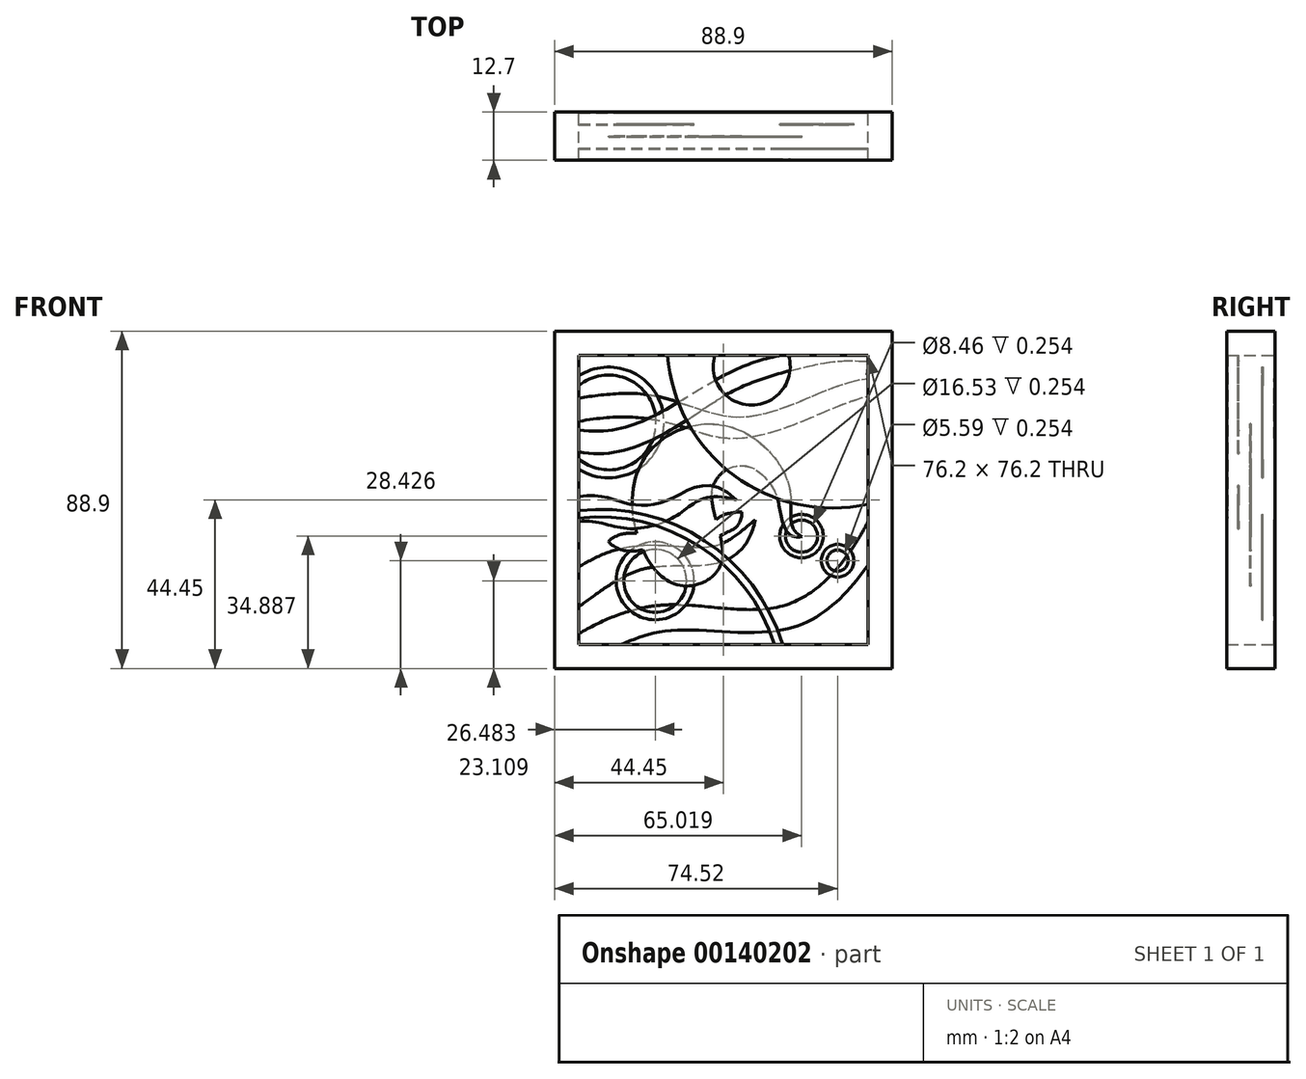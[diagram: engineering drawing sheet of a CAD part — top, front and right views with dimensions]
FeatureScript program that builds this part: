
annotation { "Feature Type Name" : "Feature", "Feature Type Description" : "" }
export const myFeature = defineFeature(function(context is Context, id is Id, definition is map)
    precondition{}
    {
        {
            var Q0;
            Q0=qCreatedBy(makeId("Front.planeOp"),FACE);
            cPlane(context, id + "F0", {"entities" : qUnion([Q0]), "cplaneType" : CPlaneType.OFFSET, "offset" : 3.17 * mm, "width" : 152.4 * mm, "height" : 152.4 * mm});
        }
        {
            var Q0;
            Q0=qCreatedBy(id+"F0.planeOp",FACE);
            cPlane(context, id + "F1", {"entities" : qUnion([Q0]), "cplaneType" : CPlaneType.OFFSET, "offset" : 3.17 * mm, "width" : 152.4 * mm, "height" : 152.4 * mm});
        }
        {
            var Q0;
            Q0=qCreatedBy(id+"F1.planeOp",FACE);
            cPlane(context, id + "F2", {"entities" : qUnion([Q0]), "cplaneType" : CPlaneType.OFFSET, "offset" : 3.17 * mm, "width" : 152.4 * mm, "height" : 152.4 * mm});
        }
        {
            var Q0;
            Q0=qCreatedBy(id+"F2.planeOp",FACE);
            cPlane(context, id + "F3", {"entities" : qUnion([Q0]), "cplaneType" : CPlaneType.OFFSET, "offset" : 3.17 * mm, "width" : 152.4 * mm, "height" : 152.4 * mm});
        }
        {
            var Q0;
            Q0=qCreatedBy(makeId("Front.planeOp"),FACE);
            var sketch = newSketch(context, id + "F4", { "sketchPlane" : qUnion([Q0])});
            skLineSegment(sketch, "E0.bottom", {"start": v(-38.1, 38.1) * mm, "end": v(38.1, 38.1) * mm});
            skLineSegment(sketch, "E0.top", {"start": v(-38.1, -38.1) * mm, "end": v(38.1, -38.1) * mm});
            skLineSegment(sketch, "E0.left", {"start": v(-38.1, 38.1) * mm, "end": v(-38.1, -38.1) * mm});
            skLineSegment(sketch, "E0.right", {"start": v(38.1, 38.1) * mm, "end": v(38.1, -38.1) * mm});
            skLineSegment(sketch, "E1", {"start": v(-38.1, 38.1) * mm, "end": v(38.1, -38.1) * mm, "construction": true});
            skFitSpline(sketch, "E2", {"points": [v(-38.1, -35.27) * mm, v(-14.25, -27.64) * mm, v(17.02, -27.5) * mm, v(38.1, -5.66) * mm], "startDerivative": vector(70.4, 40.4) * mm, "endDerivative": vector(39.04, 77.61) * mm});
            skFitSpline(sketch, "E3", {"points": [v(-38.1, -28.14) * mm, v(-20.93, -18.19) * mm, v(-1.94, -16.72) * mm, v(8.35, -5.22) * mm], "startDerivative": vector(44.97, 31.21) * mm, "endDerivative": vector(12.34, 67.57) * mm});
            skFitSpline(sketch, "E4", {"points": [v(-38.1, -17.76) * mm, v(-22.26, -12.04) * mm, v(-4.48, -12.44) * mm, v(8.35, -5.22) * mm], "startDerivative": vector(39.42, 26) * mm, "endDerivative": vector(58.43, 50.8) * mm});
            skFitSpline(sketch, "E5", {"points": [v(-38.1, 26.81) * mm, v(-18.3, 27.46) * mm, v(3.15, 21.85) * mm, v(23.34, 27.3) * mm, v(38.1, 31.97) * mm], "startDerivative": vector(68.65, 10.07) * mm, "endDerivative": vector(57.97, 5.08) * mm});
            skFitSpline(sketch, "E6", {"points": [v(-38.1, 20.65) * mm, v(1.33, 16.2) * mm, v(26.07, 22.94) * mm, v(38.1, 27.38) * mm], "startDerivative": vector(157.64, 29.2) * mm, "endDerivative": vector(59.76, 16.98) * mm});
            skFitSpline(sketch, "E7", {"points": [v(-26.89, -38.1) * mm, v(-12.74, -34.34) * mm, v(18.19, -33.63) * mm, v(38.1, -17.12) * mm], "startDerivative": vector(45.06, 18.9) * mm, "endDerivative": vector(40.9, 58.43) * mm});
            skSolve(sketch);
        }
        {
            var Q0;
            {var subQ0=sQuery(id+"F4.wireOp",EDGE,"E5");Q0=makeQuery(id+"F4.imprint","IMPRINT",FACE,{"disambiguationData":[TD([[makeQuery(id+"F4.imprint","IMPRINT",EDGE,{"derivedFrom":subQ0}),-1.0]])]});}
            var Q1;
            {var subQ0=sQuery(id+"F4.wireOp",EDGE,"E3");Q1=makeQuery(id+"F4.imprint","IMPRINT",FACE,{"disambiguationData":[TD([[makeQuery(id+"F4.imprint","IMPRINT",EDGE,{"derivedFrom":subQ0}),1.0]])]});}
            var Q2;
            {var subQ3=sQuery(id+"F4.wireOp",EDGE,"E2");Q2=makeQuery(id+"F4.imprint","IMPRINT",FACE,{"disambiguationData":[TD([[makeQuery(id+"F4.imprint","IMPRINT",EDGE,{"derivedFrom":subQ3}),-1.0]])]});}
            extrude(context, id + "F5", {"entities" : qUnion([Q0, Q1, Q2]), "depth" : 0.25 * mm});
        }
        {
            var Q0;
            Q0=qCreatedBy(makeId("Front.planeOp"),FACE);
            var sketch = newSketch(context, id + "F6", { "sketchPlane" : qUnion([Q0])});
            skLineSegment(sketch, "E8.bottom", {"start": v(-38.1, -38.1) * mm, "end": v(38.1, -38.1) * mm});
            skLineSegment(sketch, "E8.top", {"start": v(-38.1, 38.1) * mm, "end": v(38.1, 38.1) * mm});
            skLineSegment(sketch, "E8.left", {"start": v(-38.1, -38.1) * mm, "end": v(-38.1, 38.1) * mm});
            skLineSegment(sketch, "E8.right", {"start": v(38.1, -38.1) * mm, "end": v(38.1, 38.1) * mm});
            skPoint(sketch, "E8.middle", {"position": v(0, 0) * mm});
            skLineSegment(sketch, "E9.0", {"start": v(44.45, -44.45) * mm, "end": v(44.45, 44.45) * mm});
            skLineSegment(sketch, "E9.1", {"start": v(-44.45, -44.45) * mm, "end": v(44.45, -44.45) * mm});
            skLineSegment(sketch, "E9.2", {"start": v(-44.45, -44.45) * mm, "end": v(-44.45, 44.45) * mm});
            skLineSegment(sketch, "E9.3", {"start": v(-44.45, 44.45) * mm, "end": v(44.45, 44.45) * mm});
            skSolve(sketch);
        }
        {
            var Q0;
            Q0 = qSketchRegion(id + "F6", true);
            extrude(context, id + "F7", {"entities" : qUnion([Q0]), "depth" : 12.7 * mm});
        }
        {
            var Q0;
            Q0=qCreatedBy(id+"F0.planeOp",FACE);
            var sketch = newSketch(context, id + "F8", { "sketchPlane" : qUnion([Q0])});
            skArc(sketch, "E10", {"start": v(-38.1, 10.68) * mm, "mid": v(-17.75, 20.39) * mm, "end": v(-38.1, 30.1) * mm});
            skCircle(sketch, "E11", {"center": v(20.57, -9.56) * mm, "radius": 4.23 * mm});
            skCircle(sketch, "E12", {"center": v(-17.97, -21.34) * mm, "radius": 8.27 * mm});
            skCircle(sketch, "E13", {"center": v(30.07, -16.02) * mm, "radius": 2.8 * mm});
            skCircle(sketch, "E14.0", {"center": v(20.57, -9.56) * mm, "radius": 5.73 * mm});
            skCircle(sketch, "E15.0", {"center": v(30.07, -16.02) * mm, "radius": 4.3 * mm});
            skArc(sketch, "E16.0", {"start": v(-38.1, 8.1) * mm, "mid": v(-15.65, 20.39) * mm, "end": v(-38.1, 32.68) * mm});
            skCircle(sketch, "E17.0", {"center": v(-17.97, -21.34) * mm, "radius": 10.27 * mm});
            skLineSegment(sketch, "E18.0", {"start": v(-38.1, 38.1) * mm, "end": v(38.1, 38.1) * mm});
            skLineSegment(sketch, "E18.1", {"start": v(-38.1, -38.1) * mm, "end": v(-38.1, 38.1) * mm});
            skLineSegment(sketch, "E18.2", {"start": v(-38.1, -38.1) * mm, "end": v(38.1, -38.1) * mm});
            skLineSegment(sketch, "E18.3", {"start": v(38.1, -38.1) * mm, "end": v(38.1, 38.1) * mm});
            skSolve(sketch);
        }
        {
            var Q0;
            Q0=makeQuery(id+"F8.imprint","IMPRINT",FACE,{"disambiguationData":[TD([[makeQuery(id+"F8.imprint","IMPRINT",EDGE,{"derivedFrom":sQuery(id+"F8.wireOp",EDGE,"374bc7da-6bf9-40b4-b142-eb3eeef292bf")}),-1.0]])]});
            var Q1;
            Q1=makeQuery(id+"F8.imprint","IMPRINT",FACE,{"disambiguationData":[TD([[makeQuery(id+"F8.imprint","IMPRINT",EDGE,{"derivedFrom":sQuery(id+"F8.wireOp",EDGE,"3488932f-d9eb-453f-bc1f-a6e8dee0a916")}),-1.0]])]});
            var Q2;
            Q2=makeQuery(id+"F8.imprint","IMPRINT",FACE,{"disambiguationData":[TD([[makeQuery(id+"F8.imprint","IMPRINT",EDGE,{"derivedFrom":sQuery(id+"F8.wireOp",EDGE,"E11")}),-1.0]])]});
            var Q3;
            Q3=makeQuery(id+"F8.imprint","IMPRINT",FACE,{"disambiguationData":[TD([[makeQuery(id+"F8.imprint","IMPRINT",EDGE,{"derivedFrom":sQuery(id+"F8.wireOp",EDGE,"E10")}),-1.0]])]});
            var Q4;
            Q4=makeQuery(id+"F8.imprint","IMPRINT",FACE,{"disambiguationData":[TD([[makeQuery(id+"F8.imprint","IMPRINT",EDGE,{"derivedFrom":sQuery(id+"F8.wireOp",EDGE,"Zx9qhp7R-mZTL-MEG7-K4O5-H50MOL2ynZSX")}),-1.0]])]});
            var Q5;
            Q5=makeQuery(id+"F8.imprint","IMPRINT",FACE,{"disambiguationData":[TD([[makeQuery(id+"F8.imprint","IMPRINT",EDGE,{"derivedFrom":sQuery(id+"F8.wireOp",EDGE,"BIX8gzzW-vuGM-WMEv-DDVe-u0uWoqFmIHmd")}),-1.0]])]});
            var Q6;
            Q6=makeQuery(id+"F8.imprint","IMPRINT",FACE,{"disambiguationData":[TD([[makeQuery(id+"F8.imprint","IMPRINT",EDGE,{"derivedFrom":sQuery(id+"F8.wireOp",EDGE,"E13")}),-1.0]])]});
            var Q7;
            {var subQ0=sQuery(id+"F8.wireOp",EDGE,"E18.1");var subQ1=sQuery(id+"F8.wireOp",EDGE,"E12");var subQ2=makeQuery(id+"F8.imprint","INTERSECT",VERTEX,{"disambiguationData":[OD(0.0)],"derivedFrom":[subQ1,subQ0]});Q7=makeQuery(id+"F8.imprint","IMPRINT",FACE,{"disambiguationData":[TD([[makeQuery(id+"F8.imprint","IMPRINT",EDGE,{"disambiguationData":[TD([[subQ2,-1.0]])],"derivedFrom":subQ1}),-1.0]])]});}
            var Q8;
            {var subQ0=sQuery(id+"F8.wireOp",EDGE,"E18.0");var subQ1=sQuery(id+"F8.wireOp",EDGE,"KXBxtDFX-HGSY-ahhd-k1Fz-9JbAuEpx41Wu");var subQ2=makeQuery(id+"F8.imprint","INTERSECT",VERTEX,{"disambiguationData":[OD(0.0)],"derivedFrom":[subQ1,subQ0]});Q8=makeQuery(id+"F8.imprint","IMPRINT",FACE,{"disambiguationData":[TD([[makeQuery(id+"F8.imprint","IMPRINT",EDGE,{"disambiguationData":[TD([[subQ2,-1.0]])],"derivedFrom":subQ1}),-1.0]])]});}
            extrude(context, id + "F9", {"entities" : qUnion([Q0, Q1, Q2, Q3, Q4, Q5, Q6, Q7, Q8]), "depth" : 0.25 * mm});
        }
        {
            var Q0;
            Q0=qCreatedBy(id+"F1.planeOp",FACE);
            var sketch = newSketch(context, id + "F10", { "sketchPlane" : qUnion([Q0])});
            skLineSegment(sketch, "E19.0", {"start": v(-38.1, 38.1) * mm, "end": v(38.1, 38.1) * mm});
            skLineSegment(sketch, "E19.1", {"start": v(-38.1, -38.1) * mm, "end": v(-38.1, 38.1) * mm});
            skLineSegment(sketch, "E19.2", {"start": v(38.1, -38.1) * mm, "end": v(38.1, 38.1) * mm});
            skLineSegment(sketch, "E19.3", {"start": v(-38.1, -38.1) * mm, "end": v(38.1, -38.1) * mm});
            skFitSpline(sketch, "E20", {"points": [v(-6.42, -22.19) * mm, v(-24, -1.44) * mm, v(-13.84, 17.38) * mm, v(4.9, 18.1) * mm, v(17.68, 1.88) * mm, v(20.75, -9.72) * mm], "startDerivative": vector(-137.02, -44.13) * mm, "endDerivative": vector(87.33, -43.62) * mm});
            skFitSpline(sketch, "E21", {"points": [v(-6.42, -22.19) * mm, v(-3.1, 1.4) * mm, v(5.34, 9.02) * mm, v(12.73, 3.58) * mm, v(14.81, -2.37) * mm, v(20.75, -9.72) * mm], "startDerivative": vector(122.13, 45.55) * mm, "endDerivative": vector(74.84, 16.71) * mm});
            skFitSpline(sketch, "E22", {"points": [v(-0.84, -9.53) * mm, v(3.85, -6.62) * mm, v(4.8, -3.27) * mm], "startDerivative": vector(13.73, 7.77) * mm, "endDerivative": vector(-1.75, 3.87) * mm});
            skFitSpline(sketch, "E23", {"points": [v(4.8, -3.27) * mm, v(1.86, -3.53) * mm, v(-1.94, -5.3) * mm], "startDerivative": vector(-0.8, 2.13) * mm, "endDerivative": vector(-10.71, -8.86) * mm});
            skFitSpline(sketch, "E24", {"points": [v(-21.26, -13.13) * mm, v(-27.6, -12.85) * mm, v(-30.17, -11) * mm], "startDerivative": vector(-13.73, -3.26) * mm, "endDerivative": vector(0, 3.44) * mm});
            skFitSpline(sketch, "E25", {"points": [v(-30.17, -11) * mm, v(-26.85, -9.06) * mm, v(-22.84, -8.75) * mm], "startDerivative": vector(-0.28, 3.58) * mm, "endDerivative": vector(12.81, 1.43) * mm});
            skSolve(sketch);
        }
        {
            var Q0;
            Q0=makeQuery(id+"F10.imprint","IMPRINT",FACE,{"disambiguationData":[TD([[makeQuery(id+"F10.imprint","IMPRINT",EDGE,{"derivedFrom":sQuery(id+"F10.wireOp",EDGE,"E20")}),-1.0]])]});
            var Q1;
            {var subQ0=sQuery(id+"F10.wireOp",EDGE,"E24");Q1=makeQuery(id+"F10.imprint","IMPRINT",FACE,{"disambiguationData":[TD([[makeQuery(id+"F10.imprint","IMPRINT",EDGE,{"derivedFrom":subQ0}),-1.0]])]});}
            var Q2;
            {var subQ0=sQuery(id+"F10.wireOp",EDGE,"E22");Q2=makeQuery(id+"F10.imprint","IMPRINT",FACE,{"disambiguationData":[TD([[makeQuery(id+"F10.imprint","IMPRINT",EDGE,{"derivedFrom":subQ0}),1.0]])]});}
            extrude(context, id + "F11", {"entities" : qUnion([Q0, Q1, Q2]), "depth" : 0.25 * mm});
        }
        {
            var Q0;
            Q0=qCreatedBy(id+"F2.planeOp",FACE);
            var sketch = newSketch(context, id + "F12", { "sketchPlane" : qUnion([Q0])});
            skLineSegment(sketch, "E26.0", {"start": v(-38.1, -38.1) * mm, "end": v(-38.1, 38.1) * mm});
            skFitSpline(sketch, "E27", {"points": [v(-38.1, 0.88) * mm, v(-25.6, -0.9) * mm, v(-14.42, 0) * mm, v(3.41, 0) * mm], "startDerivative": vector(55.02, 8.63) * mm, "endDerivative": vector(58.16, -57.4) * mm});
            skFitSpline(sketch, "E28", {"points": [v(-38.1, -5.76) * mm, v(-25.44, -7.55) * mm, v(-11.82, -3.82) * mm, v(3.41, 0) * mm], "startDerivative": vector(44.8, 6.37) * mm, "endDerivative": vector(75.87, -21.7) * mm});
            skLineSegment(sketch, "E29.0", {"start": v(-38.1, 38.1) * mm, "end": v(38.1, 38.1) * mm});
            skFitSpline(sketch, "E30", {"points": [v(-38.1, 18.38) * mm, v(-12.88, 25.13) * mm, v(15.54, 38.1) * mm], "startDerivative": vector(63.16, -8.78) * mm, "endDerivative": vector(64.9, 10.23) * mm});
            skFitSpline(sketch, "E31", {"points": [v(-38.1, 12.71) * mm, v(-14.02, 18.26) * mm, v(3.74, 29.26) * mm, v(24.56, 35.67) * mm, v(38.1, 36.48) * mm], "startDerivative": vector(88.93, -21.1) * mm, "endDerivative": vector(101.27, -5.4) * mm});
            skLineSegment(sketch, "E32.0", {"start": v(38.1, -38.1) * mm, "end": v(38.1, 38.1) * mm});
            skPoint(sketch, "E33", {"position": v(-38.1, 0) * mm});
            skSolve(sketch);
        }
        {
            var Q0;
            {var subQ1=sQuery(id+"F12.wireOp",EDGE,"E30");Q0=makeQuery(id+"F12.imprint","IMPRINT",FACE,{"disambiguationData":[TD([[makeQuery(id+"F12.imprint","IMPRINT",EDGE,{"derivedFrom":subQ1}),-1.0]])]});}
            var Q1;
            {var subQ0=sQuery(id+"F12.wireOp",EDGE,"E27");Q1=makeQuery(id+"F12.imprint","IMPRINT",FACE,{"disambiguationData":[TD([[makeQuery(id+"F12.imprint","IMPRINT",EDGE,{"derivedFrom":subQ0}),-1.0]])]});}
            extrude(context, id + "F13", {"entities" : qUnion([Q0, Q1]), "depth" : 0.25 * mm});
        }
        {
            var Q0;
            Q0=qCreatedBy(id+"F3.planeOp",FACE);
            var sketch = newSketch(context, id + "F14", { "sketchPlane" : qUnion([Q0])});
            skLineSegment(sketch, "E34.0", {"start": v(-38.1, 38.1) * mm, "end": v(38.1, 38.1) * mm});
            skLineSegment(sketch, "E35.0", {"start": v(38.1, -38.1) * mm, "end": v(38.1, 38.1) * mm});
            skLineSegment(sketch, "E36.0", {"start": v(-38.1, -38.1) * mm, "end": v(38.1, -38.1) * mm});
            skLineSegment(sketch, "E37.0", {"start": v(-38.1, -38.1) * mm, "end": v(-38.1, 38.1) * mm});
            skCircle(sketch, "E38", {"center": v(28.77, 41.46) * mm, "radius": 43.63 * mm});
            skCircle(sketch, "E39", {"center": v(28.77, 41.46) * mm, "radius": 41.13 * mm});
            skCircle(sketch, "E40", {"center": v(7.44, 35.11) * mm, "radius": 10.15 * mm});
            skCircle(sketch, "E41", {"center": v(7.44, 35.11) * mm, "radius": 8.15 * mm});
            skCircle(sketch, "E42", {"center": v(-32.52, -52.8) * mm, "radius": 50.28 * mm});
            skCircle(sketch, "E43", {"center": v(-32.52, -52.8) * mm, "radius": 48.28 * mm});
            skSolve(sketch);
        }
        {
            var Q0;
            {var subQ0=sQuery(id+"F14.wireOp",EDGE,"E42");var subQ1=sQuery(id+"F14.wireOp",EDGE,"E36.0");var subQ2=makeQuery(id+"F14.imprint","INTERSECT",VERTEX,{"derivedFrom":[subQ1,subQ0]});Q0=makeQuery(id+"F14.imprint","IMPRINT",FACE,{"disambiguationData":[TD([[makeQuery(id+"F14.imprint","IMPRINT",EDGE,{"disambiguationData":[TD([[subQ2,1.0]])],"derivedFrom":subQ1}),1.0]])]});}
            var Q1;
            {var subQ0=sQuery(id+"F14.wireOp",EDGE,"E38");var subQ1=sQuery(id+"F14.wireOp",EDGE,"E34.0");var subQ2=makeQuery(id+"F14.imprint","INTERSECT",VERTEX,{"derivedFrom":[subQ1,subQ0]});Q1=makeQuery(id+"F14.imprint","IMPRINT",FACE,{"disambiguationData":[TD([[makeQuery(id+"F14.imprint","IMPRINT",EDGE,{"disambiguationData":[TD([[subQ2,-1.0]])],"derivedFrom":subQ1}),-1.0]])]});}
            var Q2;
            {var subQ0=sQuery(id+"F14.wireOp",EDGE,"E40");var subQ1=sQuery(id+"F14.wireOp",EDGE,"E34.0");var subQ2=makeQuery(id+"F14.imprint","INTERSECT",VERTEX,{"disambiguationData":[OD(0.0)],"derivedFrom":[subQ1,subQ0]});Q2=makeQuery(id+"F14.imprint","IMPRINT",FACE,{"disambiguationData":[TD([[makeQuery(id+"F14.imprint","IMPRINT",EDGE,{"disambiguationData":[TD([[subQ2,-1.0]])],"derivedFrom":subQ1}),-1.0]])]});}
            extrude(context, id + "F15", {"entities" : qUnion([Q0, Q1, Q2]), "oppositeDirection" : true, "depth" : 0.25 * mm});
        }
    });
